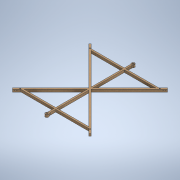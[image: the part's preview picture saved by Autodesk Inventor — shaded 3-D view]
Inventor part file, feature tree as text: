
AUTODESK INVENTOR PART (.ipt)
format: ipt  version: 2022 (Build 260153000, 153)  size: 251,904 bytes
history: native  units: mm
features: sketch x5, extrude x4, hole x2
ambient origin geometry x8: Origin, YZ Plane, XZ Plane, XY Plane, X Axis, Y Axis, Z Axis, Center Point
bodies: Body1 (feature_tree)
feature tree (11):
  sketch  "Esboço1"  dims[d5=5.0mm d6=5.0mm]
  extrude  "Extrusão2"  Depth=5.0mm
  extrude  "Extrusão3"  Depth=5.0mm
  extrude  "Extrusão4"  Depth=5.0mm
  hole  "Furo2"  [1 undecoded]
  hole  "Furo3"  [1 undecoded]
  extrude  "Extrusão5"  Depth=15.0mm
  sketch  "Esboço2"  dims[d9=5.0mm d10=5.0mm d11=5.0mm]
  sketch  "Esboço3"  dims[d12=5.0mm d15=5.0mm]
  sketch  "Esboço4"  dims[d16=5.0mm d21=5.0mm]
  sketch  "Esboço5"  dims[d22=5.0mm d27=15.0mm d28=0.0mm d33=4.0mm d34=4.0mm d35=4.0mm d36=4.0mm d37=15.0mm d38=0.0mm d39=7.0mm d40=7.0mm d41=7.0mm d42=7.0mm d43=3.0mm d44=0.0mm d52=10.0mm d53=10.0mm d54=10.0mm d55=10.0mm d56=3.0mm d57=6.0mm d58=4.0mm d59=2.0mm d60=90.0deg d61=51.2mm d62=20.594885mm d63=10.0mm d64=10.0mm d65=10.0mm d66=10.0mm d67=3.0mm d68=6.0mm d69=4.0mm d70=2.0mm d71=90.0deg d72=8.0mm d73=20.594885mm d75=15.0mm d76=3.0mm d77=40.0mm d79=360.0deg d81=20.0mm d82=15.0mm d83=3.0mm d84=40.0mm d86=360.0deg d88=15.0mm d89=0.0mm]
note: 2 required parameter values undecoded (feature->parameter linkage not recoverable at this tier; creation-order binding heuristic only, values carry confidence <= 0.55)
